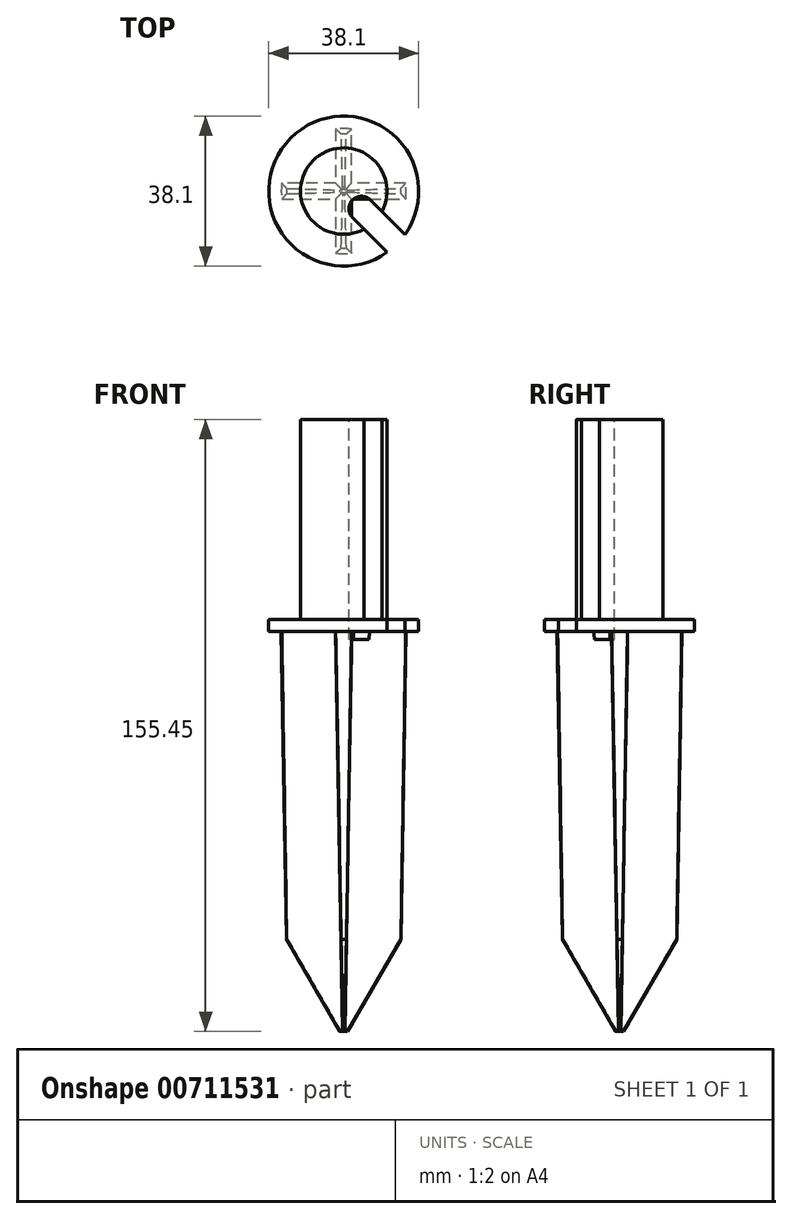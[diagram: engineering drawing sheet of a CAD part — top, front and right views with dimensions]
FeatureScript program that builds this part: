
annotation { "Feature Type Name" : "Feature", "Feature Type Description" : "" }
export const myFeature = defineFeature(function(context is Context, id is Id, definition is map)
    precondition{}
    {
        {
            var Q0;
            Q0=qCreatedBy(makeId("Top.planeOp"),FACE);
            var sketch = newSketch(context, id + "F0", { "sketchPlane" : qUnion([Q0])});
            skCircle(sketch, "E0", {"center": v(0, 0) * mm, "radius": 19.05 * mm});
            skSolve(sketch);
        }
        {
            var Q0;
            Q0 = qSketchRegion(id + "F0", true);
            extrude(context, id + "F1", {"entities" : qUnion([Q0]), "depth" : 3.05 * mm, "offsetDistance" : 25.4 * mm});
        }
        {
            var Q0;
            Q0=makeQuery(id+"F1.opExtrude","CAP_FACE",FACE,{"disambiguationData":[OSD([sQuery(id+"F0.wireOp",EDGE,"E0")])],"isStart":false});
            var sketch = newSketch(context, id + "F2", { "sketchPlane" : qUnion([Q0])});
            skCircle(sketch, "E1", {"center": v(0, 0) * mm, "radius": 10.99 * mm});
            skSolve(sketch);
        }
        {
            var Q0;
            Q0 = qSketchRegion(id + "F2", true);
            extrude(context, id + "F3", {"entities" : qUnion([Q0]), "operationType" : NewBodyOperationType.ADD, "depth" : 50.8 * mm, "offsetDistance" : 25.4 * mm});
        }
        {
            var Q0;
            Q0=makeQuery(id+"F1.opExtrude","CAP_FACE",FACE,{"disambiguationData":[OSD([sQuery(id+"F0.wireOp",EDGE,"E0")])],"isStart":true});
            var sketch = newSketch(context, id + "F4", { "sketchPlane" : qUnion([Q0])});
            skArc(sketch, "E2", {"start": v(15.74, -2.03) * mm, "mid": v(15.88, 0) * mm, "end": v(15.74, 2.03) * mm});
            skLineSegment(sketch, "E3", {"start": v(-15.88, 0) * mm, "end": v(15.88, 0) * mm, "construction": true});
            skLineSegment(sketch, "E4", {"start": v(0, 15.88) * mm, "end": v(0, -15.88) * mm, "construction": true});
            skLineSegment(sketch, "E5.0", {"start": v(-2.03, 15.74) * mm, "end": v(-2.03, 2.03) * mm});
            skLineSegment(sketch, "E6.0", {"start": v(-15.74, -2.03) * mm, "end": v(-2.03, -2.03) * mm});
            skLineSegment(sketch, "E7.0", {"start": v(2.03, 15.74) * mm, "end": v(2.03, 2.03) * mm});
            skLineSegment(sketch, "E8.0", {"start": v(-15.74, 2.03) * mm, "end": v(-2.03, 2.03) * mm});
            skArc(sketch, "E9.trimOffspring", {"start": v(-2.03, -15.74) * mm, "mid": v(0, -15.88) * mm, "end": v(2.03, -15.74) * mm});
            skArc(sketch, "E10.trimOffspring", {"start": v(2.03, 15.74) * mm, "mid": v(0, 15.88) * mm, "end": v(-2.03, 15.74) * mm});
            skArc(sketch, "E11.trimOffspring", {"start": v(-15.74, 2.03) * mm, "mid": v(-15.88, 0) * mm, "end": v(-15.74, -2.03) * mm});
            skLineSegment(sketch, "E12.trimOffspring", {"start": v(-2.03, -2.03) * mm, "end": v(-2.03, -15.74) * mm});
            skLineSegment(sketch, "E13.trimOffspring", {"start": v(2.03, 2.03) * mm, "end": v(15.74, 2.03) * mm});
            skLineSegment(sketch, "E14.trimOffspring", {"start": v(2.03, -2.03) * mm, "end": v(2.03, -15.74) * mm});
            skLineSegment(sketch, "E15.trimOffspring", {"start": v(2.03, -2.03) * mm, "end": v(15.74, -2.03) * mm});
            skSolve(sketch);
        }
        {
            var Q0;
            Q0=makeQuery(id+"F4.imprint","IMPRINT",FACE,{"disambiguationData":[TD([[makeQuery(id+"F4.imprint","IMPRINT",EDGE,{"derivedFrom":sQuery(id+"F4.wireOp",EDGE,"E2")}),1.0]])]});
            extrude(context, id + "F5", {"entities" : qUnion([Q0]), "operationType" : NewBodyOperationType.ADD, "depth" : 101.6 * mm, "offsetDistance" : 25.4 * mm, "hasDraft" : true, "draftAngle" : 1 * degree, "draftPullDirection" : true});
        }
        {
            var Q0;
            Q0=makeQuery(id+"F5.opExtrude","CAP_FACE",FACE,{"disambiguationData":[OSD([sQuery(id+"F4.wireOp",EDGE,"E2"),sQuery(id+"F4.wireOp",EDGE,"E5.0"),sQuery(id+"F4.wireOp",EDGE,"E6.0"),sQuery(id+"F4.wireOp",EDGE,"E7.0"),sQuery(id+"F4.wireOp",EDGE,"E8.0"),sQuery(id+"F4.wireOp",EDGE,"E9.trimOffspring"),sQuery(id+"F4.wireOp",EDGE,"E10.trimOffspring"),sQuery(id+"F4.wireOp",EDGE,"E11.trimOffspring"),sQuery(id+"F4.wireOp",EDGE,"E12.trimOffspring"),sQuery(id+"F4.wireOp",EDGE,"E13.trimOffspring"),sQuery(id+"F4.wireOp",EDGE,"E14.trimOffspring"),sQuery(id+"F4.wireOp",EDGE,"E15.trimOffspring")])],"isStart":false});
            var sketch = newSketch(context, id + "F6", { "sketchPlane" : qUnion([Q0])});
            skCircle(sketch, "E16", {"center": v(0, 0) * mm, "radius": 38.1 * mm});
            skCircle(sketch, "E17", {"center": v(0, 0) * mm, "radius": 1.02 * mm});
            skSolve(sketch);
        }
        {
            var Q0;
            Q0 = qSketchRegion(id + "F6", true);
            extrude(context, id + "F7", {"entities" : qUnion([Q0]), "operationType" : NewBodyOperationType.REMOVE, "oppositeDirection" : true, "depth" : 25.4 * mm, "offsetDistance" : 25.4 * mm, "hasDraft" : true, "draftAngle" : 30 * degree, "draftPullDirection" : true});
        }
        {
            var Q0;
            Q0=makeQuery(id+"F3.opExtrude","CAP_FACE",FACE,{"disambiguationData":[OSD([sQuery(id+"F2.wireOp",EDGE,"E1")])],"isStart":false});
            var sketch = newSketch(context, id + "F8", { "sketchPlane" : qUnion([Q0])});
            skArc(sketch, "E18", {"start": v(6.74, -2.25) * mm, "mid": v(2.25, -2.25) * mm, "end": v(2.25, -6.74) * mm});
            skLineSegment(sketch, "E19", {"start": v(10.99, 0) * mm, "end": v(0, 0) * mm, "construction": true});
            skLineSegment(sketch, "E20", {"start": v(4.5, -4.5) * mm, "end": v(2.25, -6.74) * mm, "construction": true});
            skLineSegment(sketch, "E21", {"start": v(2.25, -6.74) * mm, "end": v(11.04, -15.53) * mm});
            skLineSegment(sketch, "E22", {"start": v(6.74, -2.25) * mm, "end": v(15.53, -11.04) * mm});
            skLineSegment(sketch, "E23", {"start": v(0, 0) * mm, "end": v(4.5, -4.5) * mm, "construction": true});
            skLineSegment(sketch, "E24", {"start": v(4.5, -4.5) * mm, "end": v(7.77, -7.77) * mm, "construction": true});
            skArc(sketch, "E25.0", {"start": v(11.04, -15.53) * mm, "mid": v(13.47, -13.47) * mm, "end": v(15.53, -11.04) * mm});
            skSolve(sketch);
        }
        {
            var Q0;
            {var subQ0=sQuery(id+"F8.wireOp",EDGE,"E18");Q0=makeQuery(id+"F8.imprint","IMPRINT",FACE,{"disambiguationData":[TD([[makeQuery(id+"F8.imprint","IMPRINT",EDGE,{"derivedFrom":subQ0}),1.0]])]});}
            var Q1;
            {var subQ0=sQuery(id+"F8.wireOp",EDGE,"E25.0");Q1=makeQuery(id+"F8.imprint","IMPRINT",FACE,{"disambiguationData":[TD([[makeQuery(id+"F8.imprint","IMPRINT",EDGE,{"derivedFrom":subQ0}),1.0]])]});}
            extrude(context, id + "F9", {"entities" : qUnion([Q0, Q1]), "operationType" : NewBodyOperationType.REMOVE, "oppositeDirection" : true, "depth" : 55.88 * mm, "offsetDistance" : 25.4 * mm});
        }
    });
